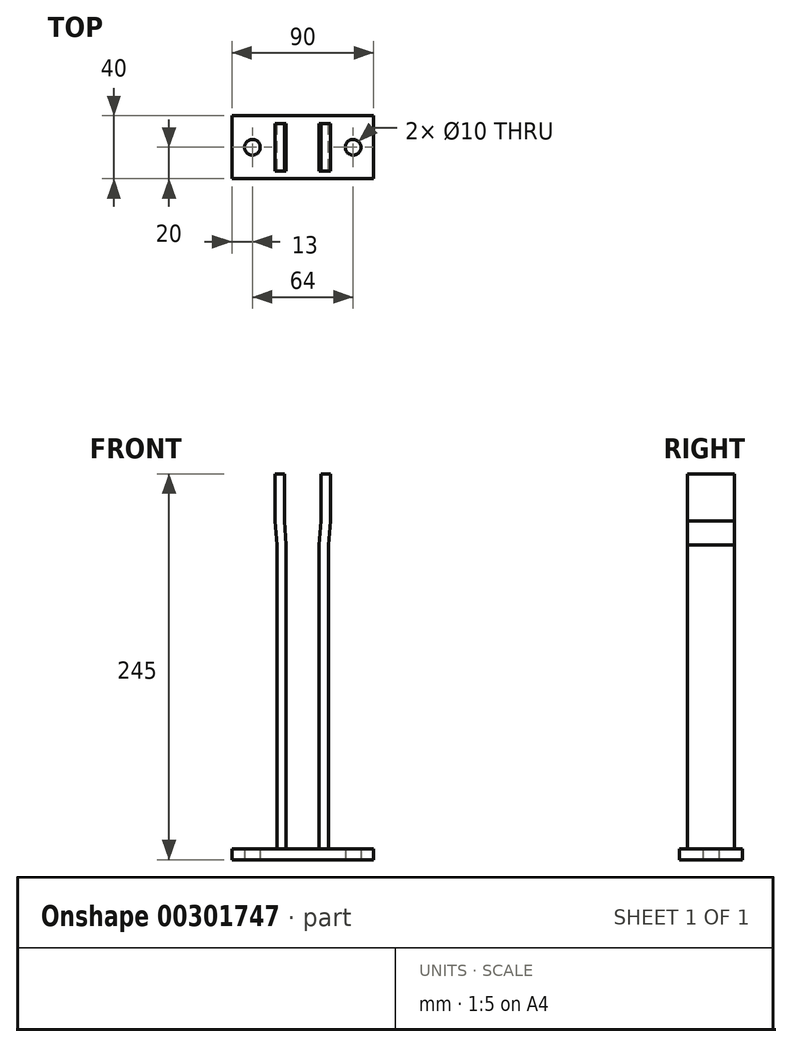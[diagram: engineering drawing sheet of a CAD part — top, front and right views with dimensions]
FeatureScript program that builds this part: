
annotation { "Feature Type Name" : "Feature", "Feature Type Description" : "" }
export const myFeature = defineFeature(function(context is Context, id is Id, definition is map)
    precondition{}
    {
        {
            var Q0;
            Q0=qCreatedBy(makeId("Right.planeOp"),FACE);
            var sketch = newSketch(context, id + "F0", { "sketchPlane" : qUnion([Q0])});
            skLineSegment(sketch, "E0.bottom", {"start": v(-20, 7) * mm, "end": v(20, 7) * mm});
            skLineSegment(sketch, "E0.left", {"start": v(-20, 7) * mm, "end": v(-20, 0) * mm});
            skLineSegment(sketch, "E0.right", {"start": v(20, 7) * mm, "end": v(20, 0) * mm});
            skLineSegment(sketch, "E1.trimOffspring", {"start": v(-20, 0) * mm, "end": v(20, 0) * mm});
            skSolve(sketch);
        }
        {
            var Q0;
            {var subQ3=sQuery(id+"F0.wireOp",EDGE,"ff7b447e-6627-4066-b775-27bb9192647b.left");Q0=makeQuery(id+"F0.imprint","IMPRINT",FACE,{"disambiguationData":[TD([[makeQuery(id+"F0.imprint","IMPRINT",EDGE,{"derivedFrom":subQ3}),-1.0]])]});}
            var Q1;
            {var subQ3=sQuery(id+"F0.wireOp",EDGE,"ff7b447e-6627-4066-b775-27bb9192647b.right");Q1=makeQuery(id+"F0.imprint","IMPRINT",FACE,{"disambiguationData":[TD([[makeQuery(id+"F0.imprint","IMPRINT",EDGE,{"derivedFrom":subQ3}),1.0]])]});}
            var Q2;
            {var subQ0=sQuery(id+"F0.wireOp",EDGE,"ff7b447e-6627-4066-b775-27bb9192647b.top");Q2=makeQuery(id+"F0.imprint","IMPRINT",FACE,{"disambiguationData":[TD([[makeQuery(id+"F0.imprint","IMPRINT",EDGE,{"derivedFrom":subQ0}),-1.0]])]});}
            var Q3;
            {var subQ5=sQuery(id+"F0.wireOp",EDGE,"E0.left");Q3=makeQuery(id+"F0.imprint","IMPRINT",FACE,{"disambiguationData":[TD([[makeQuery(id+"F0.imprint","IMPRINT",EDGE,{"derivedFrom":subQ5}),1.0]])]});}
            var Q4;
            {var subQ5=sQuery(id+"F0.wireOp",EDGE,"E0.right");Q4=makeQuery(id+"F0.imprint","IMPRINT",FACE,{"disambiguationData":[TD([[makeQuery(id+"F0.imprint","IMPRINT",EDGE,{"derivedFrom":subQ5}),-1.0]])]});}
            extrude(context, id + "F1", {"entities" : qUnion([Q0, Q1, Q2, Q3, Q4]), "depth" : 90 * mm});
        }
        {
            var Q0;
            Q0=qCreatedBy(makeId("Top.planeOp"),FACE);
            var sketch = newSketch(context, id + "F2", { "sketchPlane" : qUnion([Q0])});
            skLineSegment(sketch, "E2.bottom", {"start": v(28.5, 15) * mm, "end": v(34.5, 15) * mm});
            skLineSegment(sketch, "E2.top", {"start": v(28.5, -15) * mm, "end": v(34.5, -15) * mm});
            skLineSegment(sketch, "E2.left", {"start": v(28.5, 15) * mm, "end": v(28.5, -15) * mm});
            skLineSegment(sketch, "E2.right", {"start": v(34.5, 15) * mm, "end": v(34.5, -15) * mm});
            skLineSegment(sketch, "E3.bottom", {"start": v(55.5, 15) * mm, "end": v(61.5, 15) * mm});
            skLineSegment(sketch, "E3.top", {"start": v(55.5, -15) * mm, "end": v(61.5, -15) * mm});
            skLineSegment(sketch, "E3.left", {"start": v(55.5, 15) * mm, "end": v(55.5, -15) * mm});
            skLineSegment(sketch, "E3.right", {"start": v(61.5, 15) * mm, "end": v(61.5, -15) * mm});
            skLineSegment(sketch, "E4", {"start": v(0, -20) * mm, "end": v(90, -20) * mm, "construction": true});
            skLineSegment(sketch, "E5", {"start": v(90, 20) * mm, "end": v(90, -20) * mm, "construction": true});
            skPoint(sketch, "E6.center.orphan", {"position": v(77, 0) * mm});
            skPoint(sketch, "E7.center.orphan", {"position": v(13, 0) * mm});
            skSolve(sketch);
        }
        {
            var Q0;
            Q0=qCreatedBy(makeId("Top.planeOp"),FACE);
            var sketch = newSketch(context, id + "F3", { "sketchPlane" : qUnion([Q0])});
            skCircle(sketch, "E8", {"center": v(77, 0) * mm, "radius": 5 * mm});
            skCircle(sketch, "E9", {"center": v(13, 0) * mm, "radius": 5 * mm});
            skSolve(sketch);
        }
        {
            var Q0;
            Q0=sQuery(id+"F3.wireOp",VERTEX,"E9.center");
            var Q1;
            Q1=sQuery(id+"F3.wireOp",VERTEX,"E8.center");
            var Q2;
            Q2=makeQuery(id+"F1.opExtrude","SWEPT_BODY",BODY,{"disambiguationData":[OSD([sQuery(id+"F0.wireOp",EDGE,"E0.bottom"),sQuery(id+"F0.wireOp",EDGE,"E0.left"),sQuery(id+"F0.wireOp",EDGE,"E0.right"),sQuery(id+"F0.wireOp",EDGE,"E1.trimOffspring")])]});
            hole(context, id + "F4", {"style" : HoleStyle.SIMPLE, "endStyle" : HoleEndStyle.THROUGH, "oppositeDirection" : true, "holeDiameter" : 10 * mm, "tappedDepth" : 12 * mm, "tapClearance" : 3, "locations" : qUnion([Q0, Q1]), "scope" : qUnion([Q2])});
        }
        {
            var Q0;
            Q0=qCreatedBy(makeId("Front.planeOp"),FACE);
            var sketch = newSketch(context, id + "F5", { "sketchPlane" : qUnion([Q0])});
            skLineSegment(sketch, "E10.bottom", {"start": v(28.5, 200) * mm, "end": v(34.5, 200) * mm});
            skLineSegment(sketch, "E10.top", {"start": v(28.5, 0) * mm, "end": v(34.5, 0) * mm});
            skLineSegment(sketch, "E10.left", {"start": v(28.5, 200) * mm, "end": v(28.5, 0) * mm});
            skLineSegment(sketch, "E10.right", {"start": v(34.5, 200) * mm, "end": v(34.5, 0) * mm});
            skLineSegment(sketch, "E11.bottom", {"start": v(55.5, 200) * mm, "end": v(61.5, 200) * mm});
            skLineSegment(sketch, "E11.top", {"start": v(55.5, 0) * mm, "end": v(61.5, 0) * mm});
            skLineSegment(sketch, "E11.left", {"start": v(55.5, 200) * mm, "end": v(55.5, 0) * mm});
            skLineSegment(sketch, "E11.right", {"start": v(61.5, 200) * mm, "end": v(61.5, 0) * mm});
            skLineSegment(sketch, "E12.bottom", {"start": v(56.5, 215) * mm, "end": v(62.5, 215) * mm});
            skLineSegment(sketch, "E12.top", {"start": v(56.5, 245) * mm, "end": v(62.5, 245) * mm});
            skLineSegment(sketch, "E12.left", {"start": v(56.5, 215) * mm, "end": v(56.5, 245) * mm});
            skLineSegment(sketch, "E12.right", {"start": v(62.5, 215) * mm, "end": v(62.5, 245) * mm});
            skLineSegment(sketch, "E13.bottom", {"start": v(33.5, 215) * mm, "end": v(27.5, 215) * mm});
            skLineSegment(sketch, "E13.top", {"start": v(33.5, 245) * mm, "end": v(27.5, 245) * mm});
            skLineSegment(sketch, "E13.left", {"start": v(33.5, 215) * mm, "end": v(33.5, 245) * mm});
            skLineSegment(sketch, "E13.right", {"start": v(27.5, 215) * mm, "end": v(27.5, 245) * mm});
            skLineSegment(sketch, "E14", {"start": v(27.5, 215) * mm, "end": v(28.5, 200) * mm});
            skLineSegment(sketch, "E15", {"start": v(33.5, 215) * mm, "end": v(34.5, 200) * mm});
            skLineSegment(sketch, "E16", {"start": v(56.5, 215) * mm, "end": v(55.5, 200) * mm});
            skLineSegment(sketch, "E17", {"start": v(62.5, 215) * mm, "end": v(61.5, 200) * mm});
            skLineSegment(sketch, "E18", {"start": v(61.5, 200) * mm, "end": v(61.5, 254.73) * mm, "construction": true});
            skLineSegment(sketch, "E19", {"start": v(34.5, 200) * mm, "end": v(34.5, 253.81) * mm, "construction": true});
            skLineSegment(sketch, "E20", {"start": v(28.5, 200) * mm, "end": v(28.5, 253.23) * mm, "construction": true});
            skLineSegment(sketch, "E21", {"start": v(55.5, 200) * mm, "end": v(55.5, 255.1) * mm, "construction": true});
            skSolve(sketch);
        }
        {
            var Q0;
            Q0=makeQuery(id+"F5.imprint","IMPRINT",FACE,{"disambiguationData":[TD([[makeQuery(id+"F5.imprint","IMPRINT",EDGE,{"derivedFrom":sQuery(id+"F5.wireOp",EDGE,"E12.bottom")}),1.0]])]});
            var Q1;
            Q1=makeQuery(id+"F5.imprint","IMPRINT",FACE,{"disambiguationData":[TD([[makeQuery(id+"F5.imprint","IMPRINT",EDGE,{"derivedFrom":sQuery(id+"F5.wireOp",EDGE,"E11.bottom")}),1.0]])]});
            var Q2;
            Q2=makeQuery(id+"F5.imprint","IMPRINT",FACE,{"disambiguationData":[TD([[makeQuery(id+"F5.imprint","IMPRINT",EDGE,{"derivedFrom":sQuery(id+"F5.wireOp",EDGE,"E11.bottom")}),-1.0]])]});
            var Q3;
            Q3=makeQuery(id+"F5.imprint","IMPRINT",FACE,{"disambiguationData":[TD([[makeQuery(id+"F5.imprint","IMPRINT",EDGE,{"derivedFrom":sQuery(id+"F5.wireOp",EDGE,"E10.bottom")}),-1.0]])]});
            var Q4;
            Q4=makeQuery(id+"F5.imprint","IMPRINT",FACE,{"disambiguationData":[TD([[makeQuery(id+"F5.imprint","IMPRINT",EDGE,{"derivedFrom":sQuery(id+"F5.wireOp",EDGE,"E10.bottom")}),1.0]])]});
            var Q5;
            Q5=makeQuery(id+"F5.imprint","IMPRINT",FACE,{"disambiguationData":[TD([[makeQuery(id+"F5.imprint","IMPRINT",EDGE,{"derivedFrom":sQuery(id+"F5.wireOp",EDGE,"E13.bottom")}),-1.0]])]});
            extrude(context, id + "F6", {"entities" : qUnion([Q0, Q1, Q2, Q3, Q4, Q5]), "operationType" : NewBodyOperationType.ADD, "depth" : 15 * mm});
        }
        {
            var Q0;
            Q0=makeQuery(id+"F6.opExtrude","CAP_FACE",FACE,{"disambiguationData":[OSD([sQuery(id+"F5.wireOp",EDGE,"E10.top"),sQuery(id+"F5.wireOp",EDGE,"E10.left"),sQuery(id+"F5.wireOp",EDGE,"E10.right"),sQuery(id+"F5.wireOp",EDGE,"E13.top"),sQuery(id+"F5.wireOp",EDGE,"E13.left"),sQuery(id+"F5.wireOp",EDGE,"E13.right"),sQuery(id+"F5.wireOp",EDGE,"E14"),sQuery(id+"F5.wireOp",EDGE,"E15")])],"isStart":true});
            var Q1;
            Q1=makeQuery(id+"F6.opExtrude","CAP_FACE",FACE,{"disambiguationData":[OSD([sQuery(id+"F5.wireOp",EDGE,"E11.top"),sQuery(id+"F5.wireOp",EDGE,"E11.left"),sQuery(id+"F5.wireOp",EDGE,"E11.right"),sQuery(id+"F5.wireOp",EDGE,"E12.top"),sQuery(id+"F5.wireOp",EDGE,"E12.left"),sQuery(id+"F5.wireOp",EDGE,"E12.right"),sQuery(id+"F5.wireOp",EDGE,"E16"),sQuery(id+"F5.wireOp",EDGE,"E17")])],"isStart":true});
            extrude(context, id + "F7", {"entities" : qUnion([Q0, Q1]), "operationType" : NewBodyOperationType.ADD, "depth" : 15 * mm});
        }
    });
